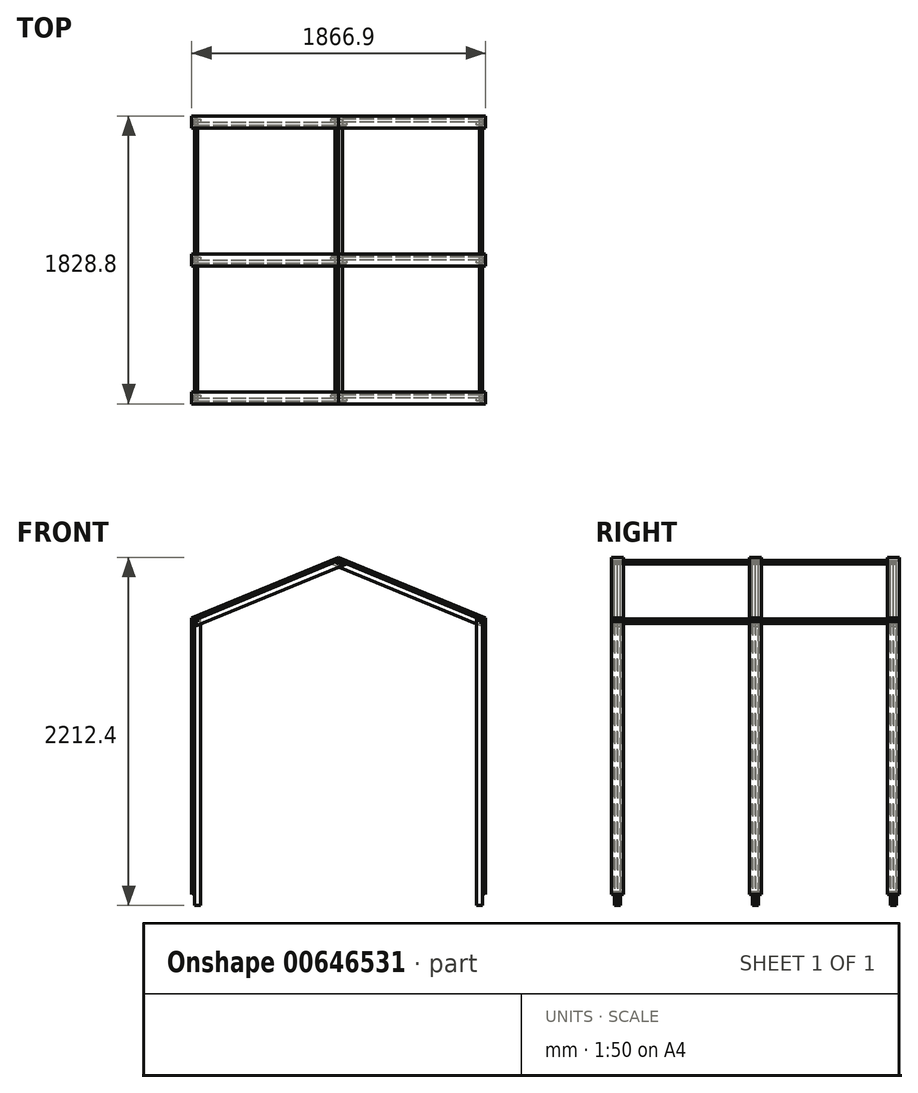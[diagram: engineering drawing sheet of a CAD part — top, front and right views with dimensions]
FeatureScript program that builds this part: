
annotation { "Feature Type Name" : "Feature", "Feature Type Description" : "" }
export const myFeature = defineFeature(function(context is Context, id is Id, definition is map)
    precondition{}
    {
        {
            var Q0;
            Q0=qCreatedBy(makeId("Front.planeOp"),FACE);
            var sketch = newSketch(context, id + "F0", { "sketchPlane" : qUnion([Q0])});
            skLineSegment(sketch, "E0", {"start": v(-914.4, 0) * mm, "end": v(914.4, 0) * mm, "construction": true});
            skLineSegment(sketch, "E1", {"start": v(914.4, 0) * mm, "end": v(914.4, -378.76) * mm, "construction": true});
            skLineSegment(sketch, "E2", {"start": v(914.4, -378.76) * mm, "end": v(-914.4, -378.76) * mm, "construction": true});
            skLineSegment(sketch, "E3", {"start": v(-914.4, -378.76) * mm, "end": v(-914.4, 0) * mm, "construction": true});
            skLineSegment(sketch, "E4", {"start": v(914.4, -378.76) * mm, "end": v(0, 0) * mm});
            skLineSegment(sketch, "E5", {"start": v(0, 0) * mm, "end": v(-914.4, -378.76) * mm, "construction": true});
            skLineSegment(sketch, "E6", {"start": v(914.4, -378.76) * mm, "end": v(914.4, -420) * mm});
            skLineSegment(sketch, "E7", {"start": v(914.4, -420) * mm, "end": v(-49.78, -20.62) * mm});
            skLineSegment(sketch, "E8", {"start": v(-49.78, -20.62) * mm, "end": v(0, 0) * mm});
            skSolve(sketch);
        }
        {
            var Q0;
            Q0=makeQuery(id+"F0.imprint","IMPRINT",FACE,{"disambiguationData":[TD([[makeQuery(id+"F0.imprint","IMPRINT",EDGE,{"derivedFrom":sQuery(id+"F0.wireOp",EDGE,"E4")}),1.0]])]});
            extrude(context, id + "F1", {"entities" : qUnion([Q0]), "depth" : 19.05 * mm, "offsetDistance" : 25.4 * mm});
        }
        {
            var Q0;
            Q0=makeQuery(id+"F1.opExtrude","SWEPT_BODY",BODY,{"disambiguationData":[OSD([sQuery(id+"F0.wireOp",EDGE,"E4"),sQuery(id+"F0.wireOp",EDGE,"E6"),sQuery(id+"F0.wireOp",EDGE,"E7"),sQuery(id+"F0.wireOp",EDGE,"E8")])]});
            var Q1;
            Q1=makeQuery(id+"F1.opExtrude","CAP_VERTEX",VERTEX,{"disambiguationData":[OSD([sQuery(id+"F0.wireOp",EDGE,"E4"),sQuery(id+"F0.wireOp",EDGE,"E6")])],"isStart":true});
            var Q2;
            Q2=makeQuery(id+"F1.opExtrude","CAP_VERTEX",VERTEX,{"disambiguationData":[OSD([sQuery(id+"F0.wireOp",EDGE,"E4"),sQuery(id+"F0.wireOp",EDGE,"E6")])],"isStart":false});
            var Q3;
            Q3=makeQuery(id+"F1.opExtrude","CAP_EDGE",EDGE,{"disambiguationData":[OSD([sQuery(id+"F0.wireOp",EDGE,"E6")])],"isStart":false});
            transform(context, id + "F2", {"entities" : qUnion([Q0]), "transformType" : TransformType.ROTATION, "transformAxis" : qUnion([Q3]), "angle" : 180 * degree, "makeCopy" : true});
        }
        {
            var Q0;
            Q0=makeQuery(id+"F2.opPattern","COPY",BODY,{"derivedFrom":makeQuery(id+"F1.opExtrude","SWEPT_BODY",BODY,{"disambiguationData":[OSD([sQuery(id+"F0.wireOp",EDGE,"E4"),sQuery(id+"F0.wireOp",EDGE,"E6"),sQuery(id+"F0.wireOp",EDGE,"E7"),sQuery(id+"F0.wireOp",EDGE,"E8")])]}),"instanceName":"1"});
            var Q1;
            Q1=makeQuery(id+"F2.opPattern","COPY",VERTEX,{"derivedFrom":makeQuery(id+"F1.opExtrude","CAP_VERTEX",VERTEX,{"disambiguationData":[OSD([sQuery(id+"F0.wireOp",EDGE,"E4"),sQuery(id+"F0.wireOp",EDGE,"E8")])],"isStart":false}),"instanceName":"1"});
            var Q2;
            Q2=makeQuery(id+"F1.opExtrude","CAP_VERTEX",VERTEX,{"disambiguationData":[OSD([sQuery(id+"F0.wireOp",EDGE,"E4"),sQuery(id+"F0.wireOp",EDGE,"E8")])],"isStart":false});
            transform(context, id + "F3", {"entities" : qUnion([Q0]), "transformType" : TransformType.TRANSLATION_ENTITY, "oppositeDirectionEntity" : false, "transformLine" : qUnion([Q1, Q2]), "makeCopy" : false});
        }
        {
            var Q0;
            Q0=makeQuery(id+"F1.opExtrude","CAP_FACE",FACE,{"disambiguationData":[OSD([sQuery(id+"F0.wireOp",EDGE,"E4"),sQuery(id+"F0.wireOp",EDGE,"E6"),sQuery(id+"F0.wireOp",EDGE,"E7"),sQuery(id+"F0.wireOp",EDGE,"E8")])],"isStart":false});
            var sketch = newSketch(context, id + "F4", { "sketchPlane" : qUnion([Q0])});
            skLineSegment(sketch, "E9", {"start": v(914.4, -378.76) * mm, "end": v(914.4, -2191.78) * mm});
            skLineSegment(sketch, "E10", {"start": v(914.4, -2191.78) * mm, "end": v(876.3, -2191.78) * mm});
            skLineSegment(sketch, "E11", {"start": v(876.3, -2191.78) * mm, "end": v(876.3, -362.98) * mm});
            skLineSegment(sketch, "E12", {"start": v(876.3, -362.98) * mm, "end": v(914.4, -378.76) * mm});
            skSolve(sketch);
        }
        {
            var Q0;
            {var subQ3=sQuery(id+"F4.wireOp",EDGE,"E10");Q0=makeQuery(id+"F4.imprint","IMPRINT",FACE,{"disambiguationData":[TD([[makeQuery(id+"F4.imprint","IMPRINT",EDGE,{"derivedFrom":subQ3}),-1.0]])]});}
            var Q1;
            {var subQ0=sQuery(id+"F4.wireOp",EDGE,"E12");Q1=makeQuery(id+"F4.imprint","IMPRINT",FACE,{"disambiguationData":[TD([[makeQuery(id+"F4.imprint","IMPRINT",EDGE,{"derivedFrom":subQ0}),1.0]])]});}
            extrude(context, id + "F5", {"entities" : qUnion([Q0, Q1]), "depth" : 19.05 * mm, "offsetDistance" : 25.4 * mm});
        }
        {
            var Q0;
            Q0=makeQuery(id+"F5.opExtrude","SWEPT_BODY",BODY,{"disambiguationData":[OSD([sQuery(id+"F4.wireOp",EDGE,"E9"),sQuery(id+"F4.wireOp",EDGE,"E10"),sQuery(id+"F4.wireOp",EDGE,"E11"),sQuery(id+"F4.wireOp",EDGE,"E12")])]});
            var Q1;
            Q1=makeQuery(id+"F5.opExtrude","CAP_EDGE",EDGE,{"disambiguationData":[OSD([sQuery(id+"F4.wireOp",EDGE,"E9")])],"isStart":true});
            transform(context, id + "F6", {"entities" : qUnion([Q0]), "transformType" : TransformType.ROTATION, "transformAxis" : qUnion([Q1]), "angle" : 180 * degree, "makeCopy" : true});
        }
        {
            var Q0;
            Q0=makeQuery(id+"F6.opPattern","COPY",BODY,{"derivedFrom":makeQuery(id+"F5.opExtrude","SWEPT_BODY",BODY,{"disambiguationData":[OSD([sQuery(id+"F4.wireOp",EDGE,"E9"),sQuery(id+"F4.wireOp",EDGE,"E10"),sQuery(id+"F4.wireOp",EDGE,"E11"),sQuery(id+"F4.wireOp",EDGE,"E12")])]}),"instanceName":"1"});
            var Q1;
            Q1=makeQuery(id+"F5.opExtrude","CAP_VERTEX",VERTEX,{"disambiguationData":[OSD([sQuery(id+"F4.wireOp",EDGE,"E9"),sQuery(id+"F4.wireOp",EDGE,"E12")])],"isStart":true});
            var Q2;
            Q2=makeQuery(id+"F2.opPattern","COPY",VERTEX,{"derivedFrom":makeQuery(id+"F1.opExtrude","CAP_VERTEX",VERTEX,{"disambiguationData":[OSD([sQuery(id+"F0.wireOp",EDGE,"E4"),sQuery(id+"F0.wireOp",EDGE,"E6")])],"isStart":false}),"instanceName":"1"});
            transform(context, id + "F7", {"entities" : qUnion([Q0]), "transformType" : TransformType.TRANSLATION_ENTITY, "oppositeDirectionEntity" : false, "transformLine" : qUnion([Q1, Q2]), "makeCopy" : false});
        }
        {
            var Q0;
            Q0=qCreatedBy(makeId("Front.planeOp"),FACE);
            var sketch = newSketch(context, id + "F8", { "sketchPlane" : qUnion([Q0])});
            skLineSegment(sketch, "E13.0", {"start": v(914.4, -378.76) * mm, "end": v(914.4, -2191.78) * mm});
            skLineSegment(sketch, "E14.0", {"start": v(914.4, -378.76) * mm, "end": v(0, 0) * mm});
            skLineSegment(sketch, "E15.0", {"start": v(-914.4, -378.76) * mm, "end": v(0, 0) * mm});
            skLineSegment(sketch, "E16.0", {"start": v(-914.4, -378.76) * mm, "end": v(-914.4, -2191.78) * mm});
            skLineSegment(sketch, "E17", {"start": v(914.4, -2191.78) * mm, "end": v(933.45, -2191.78) * mm});
            skLineSegment(sketch, "E18", {"start": v(933.45, -2191.78) * mm, "end": v(933.45, -2121.93) * mm});
            skLineSegment(sketch, "E19", {"start": v(933.45, -2121.93) * mm, "end": v(914.4, -2102.88) * mm});
            skLineSegment(sketch, "E20", {"start": v(933.45, -2121.93) * mm, "end": v(933.45, -386.65) * mm});
            skLineSegment(sketch, "E21", {"start": v(933.45, -386.65) * mm, "end": v(914.4, -378.76) * mm});
            skLineSegment(sketch, "E22", {"start": v(933.45, -386.65) * mm, "end": v(933.45, -366.03) * mm});
            skLineSegment(sketch, "E23", {"start": v(933.45, -366.03) * mm, "end": v(0, 20.62) * mm});
            skLineSegment(sketch, "E24", {"start": v(0, 20.62) * mm, "end": v(0, 0) * mm});
            skSolve(sketch);
        }
        {
            var Q0;
            Q0=makeQuery(id+"F8.imprint","IMPRINT",FACE,{"disambiguationData":[TD([[makeQuery(id+"F8.imprint","IMPRINT",EDGE,{"derivedFrom":sQuery(id+"F8.wireOp",EDGE,"E14.0")}),-1.0]])]});
            extrude(context, id + "F9", {"entities" : qUnion([Q0]), "depth" : 76.2 * mm, "offsetDistance" : 25.4 * mm});
        }
        {
            var Q0;
            {var subQ2=sQuery(id+"F8.wireOp",EDGE,"E19");Q0=makeQuery(id+"F8.imprint","IMPRINT",FACE,{"disambiguationData":[TD([[makeQuery(id+"F8.imprint","IMPRINT",EDGE,{"derivedFrom":subQ2}),-1.0]])]});}
            extrude(context, id + "F10", {"entities" : qUnion([Q0]), "depth" : 76.2 * mm, "offsetDistance" : 25.4 * mm});
        }
        {
            var Q0;
            Q0=makeQuery(id+"F9.opExtrude","SWEPT_BODY",BODY,{"disambiguationData":[OSD([sQuery(id+"F8.wireOp",EDGE,"E14.0"),sQuery(id+"F8.wireOp",EDGE,"E21"),sQuery(id+"F8.wireOp",EDGE,"E22"),sQuery(id+"F8.wireOp",EDGE,"E23"),sQuery(id+"F8.wireOp",EDGE,"E24")])]});
            var Q1;
            Q1=makeQuery(id+"F10.opExtrude","SWEPT_BODY",BODY,{"disambiguationData":[OSD([sQuery(id+"F8.wireOp",EDGE,"E13.0"),sQuery(id+"F8.wireOp",EDGE,"E19"),sQuery(id+"F8.wireOp",EDGE,"E20"),sQuery(id+"F8.wireOp",EDGE,"E21")])]});
            var Q2;
            Q2=sQuery(id+"F8.wireOp",EDGE,"E24");
            transform(context, id + "F11", {"entities" : qUnion([Q0, Q1]), "transformType" : TransformType.ROTATION, "transformAxis" : qUnion([Q2]), "angle" : 180 * degree, "makeCopy" : true});
        }
        {
            var Q0;
            Q0=makeQuery(id+"F11.opPattern","COPY",BODY,{"derivedFrom":makeQuery(id+"F10.opExtrude","SWEPT_BODY",BODY,{"disambiguationData":[OSD([sQuery(id+"F8.wireOp",EDGE,"E13.0"),sQuery(id+"F8.wireOp",EDGE,"E19"),sQuery(id+"F8.wireOp",EDGE,"E20"),sQuery(id+"F8.wireOp",EDGE,"E21")])]}),"instanceName":"1"});
            var Q1;
            Q1=makeQuery(id+"F11.opPattern","COPY",BODY,{"derivedFrom":makeQuery(id+"F9.opExtrude","SWEPT_BODY",BODY,{"disambiguationData":[OSD([sQuery(id+"F8.wireOp",EDGE,"E14.0"),sQuery(id+"F8.wireOp",EDGE,"E21"),sQuery(id+"F8.wireOp",EDGE,"E22"),sQuery(id+"F8.wireOp",EDGE,"E23"),sQuery(id+"F8.wireOp",EDGE,"E24")])]}),"instanceName":"1"});
            var Q2;
            Q2=sQuery(id+"F8.wireOp",VERTEX,"E24.start");
            var Q3;
            Q3=makeQuery(id+"F9.opExtrude","CAP_VERTEX",VERTEX,{"disambiguationData":[OSD([sQuery(id+"F8.wireOp",EDGE,"E23"),sQuery(id+"F8.wireOp",EDGE,"E24")])],"isStart":false});
            transform(context, id + "F12", {"entities" : qUnion([Q0, Q1]), "transformType" : TransformType.TRANSLATION_ENTITY, "oppositeDirectionEntity" : false, "transformLine" : qUnion([Q2, Q3]), "makeCopy" : false});
        }
        {
            var Q0;
            Q0=makeQuery(id+"F11.opPattern","COPY",BODY,{"derivedFrom":makeQuery(id+"F10.opExtrude","SWEPT_BODY",BODY,{"disambiguationData":[OSD([sQuery(id+"F8.wireOp",EDGE,"E13.0"),sQuery(id+"F8.wireOp",EDGE,"E19"),sQuery(id+"F8.wireOp",EDGE,"E20"),sQuery(id+"F8.wireOp",EDGE,"E21")])]}),"instanceName":"1"});
            var Q1;
            Q1=makeQuery(id+"F11.opPattern","COPY",BODY,{"derivedFrom":makeQuery(id+"F9.opExtrude","SWEPT_BODY",BODY,{"disambiguationData":[OSD([sQuery(id+"F8.wireOp",EDGE,"E14.0"),sQuery(id+"F8.wireOp",EDGE,"E21"),sQuery(id+"F8.wireOp",EDGE,"E22"),sQuery(id+"F8.wireOp",EDGE,"E23"),sQuery(id+"F8.wireOp",EDGE,"E24")])]}),"instanceName":"1"});
            var Q2;
            Q2=makeQuery(id+"F10.opExtrude","SWEPT_BODY",BODY,{"disambiguationData":[OSD([sQuery(id+"F8.wireOp",EDGE,"E13.0"),sQuery(id+"F8.wireOp",EDGE,"E19"),sQuery(id+"F8.wireOp",EDGE,"E20"),sQuery(id+"F8.wireOp",EDGE,"E21")])]});
            var Q3;
            Q3=makeQuery(id+"F9.opExtrude","SWEPT_BODY",BODY,{"disambiguationData":[OSD([sQuery(id+"F8.wireOp",EDGE,"E14.0"),sQuery(id+"F8.wireOp",EDGE,"E21"),sQuery(id+"F8.wireOp",EDGE,"E22"),sQuery(id+"F8.wireOp",EDGE,"E23"),sQuery(id+"F8.wireOp",EDGE,"E24")])]});
            transform(context, id + "F13", {"entities" : qUnion([Q0, Q1, Q2, Q3]), "transformType" : TransformType.TRANSLATION_3D, "dx" : 0 * mm, "dy" : 19.05 * mm, "dz" : 0 * mm, "makeCopy" : false});
        }
        {
            var Q0;
            Q0=makeQuery(id+"F2.opPattern","COPY",FACE,{"derivedFrom":makeQuery(id+"F1.opExtrude","CAP_FACE",FACE,{"disambiguationData":[OSD([sQuery(id+"F0.wireOp",EDGE,"E4"),sQuery(id+"F0.wireOp",EDGE,"E6"),sQuery(id+"F0.wireOp",EDGE,"E7"),sQuery(id+"F0.wireOp",EDGE,"E8")])],"isStart":true}),"instanceName":"1"});
            var sketch = newSketch(context, id + "F14", { "sketchPlane" : qUnion([Q0])});
            skLineSegment(sketch, "E25", {"start": v(0, 0) * mm, "end": v(-24.9, -10.3) * mm});
            skLineSegment(sketch, "E26", {"start": v(-24.9, -10.3) * mm, "end": v(0, -20.62) * mm});
            skLineSegment(sketch, "E27", {"start": v(0, -20.62) * mm, "end": v(24.9, -10.3) * mm});
            skPoint(sketch, "E27.endSnap0", {"position": v(24.9, -10.3) * mm});
            skLineSegment(sketch, "E28", {"start": v(24.9, -10.3) * mm, "end": v(0, 0) * mm});
            skSolve(sketch);
        }
        {
            var Q0;
            Q0=makeQuery(id+"F14.imprint","IMPRINT",FACE,{"disambiguationData":[TD([[makeQuery(id+"F14.imprint","IMPRINT",EDGE,{"derivedFrom":sQuery(id+"F14.wireOp",EDGE,"E25")}),-1.0]])]});
            extrude(context, id + "F15", {"entities" : qUnion([Q0]), "operationType" : NewBodyOperationType.REMOVE, "endBound" : BoundingType.THROUGH_ALL, "oppositeDirection" : true, "depth" : 25.4 * mm, "offsetDistance" : 25.4 * mm});
        }
        {
            var Q0;
            Q0=makeQuery(id+"F5.opExtrude","CAP_FACE",FACE,{"disambiguationData":[OSD([sQuery(id+"F4.wireOp",EDGE,"E9"),sQuery(id+"F4.wireOp",EDGE,"E10"),sQuery(id+"F4.wireOp",EDGE,"E11"),sQuery(id+"F4.wireOp",EDGE,"E12")])],"isStart":false});
            var sketch = newSketch(context, id + "F16", { "sketchPlane" : qUnion([Q0])});
            skLineSegment(sketch, "E29", {"start": v(914.4, -378.76) * mm, "end": v(895.35, -370.87) * mm});
            skLineSegment(sketch, "E30", {"start": v(895.35, -370.87) * mm, "end": v(895.35, -391.49) * mm});
            skLineSegment(sketch, "E31", {"start": v(895.35, -391.49) * mm, "end": v(914.4, -399.38) * mm});
            skLineSegment(sketch, "E32", {"start": v(914.4, -399.38) * mm, "end": v(914.4, -378.76) * mm});
            skSolve(sketch);
        }
        {
            var Q0;
            Q0=makeQuery(id+"F16.imprint","IMPRINT",FACE,{"disambiguationData":[TD([[makeQuery(id+"F16.imprint","IMPRINT",EDGE,{"derivedFrom":sQuery(id+"F16.wireOp",EDGE,"E29")}),1.0]])]});
            extrude(context, id + "F17", {"entities" : qUnion([Q0]), "operationType" : NewBodyOperationType.REMOVE, "endBound" : BoundingType.THROUGH_ALL, "oppositeDirection" : true, "depth" : 25.4 * mm, "offsetDistance" : 25.4 * mm});
        }
        {
            var Q0;
            Q0=makeQuery(id+"F6.opPattern","COPY",FACE,{"derivedFrom":makeQuery(id+"F5.opExtrude","CAP_FACE",FACE,{"disambiguationData":[OSD([sQuery(id+"F4.wireOp",EDGE,"E9"),sQuery(id+"F4.wireOp",EDGE,"E10"),sQuery(id+"F4.wireOp",EDGE,"E11"),sQuery(id+"F4.wireOp",EDGE,"E12")])],"isStart":false}),"instanceName":"1"});
            var sketch = newSketch(context, id + "F18", { "sketchPlane" : qUnion([Q0])});
            skLineSegment(sketch, "E33", {"start": v(914.4, -378.76) * mm, "end": v(895.35, -370.87) * mm});
            skLineSegment(sketch, "E34", {"start": v(895.35, -370.87) * mm, "end": v(895.35, -391.49) * mm});
            skLineSegment(sketch, "E35", {"start": v(895.35, -391.49) * mm, "end": v(914.4, -399.38) * mm});
            skLineSegment(sketch, "E36", {"start": v(914.4, -399.38) * mm, "end": v(914.4, -378.76) * mm});
            skSolve(sketch);
        }
        {
            var Q0;
            Q0=makeQuery(id+"F18.imprint","IMPRINT",FACE,{"disambiguationData":[TD([[makeQuery(id+"F18.imprint","IMPRINT",EDGE,{"derivedFrom":sQuery(id+"F18.wireOp",EDGE,"E33")}),1.0]])]});
            extrude(context, id + "F19", {"entities" : qUnion([Q0]), "operationType" : NewBodyOperationType.REMOVE, "endBound" : BoundingType.THROUGH_ALL, "oppositeDirection" : true, "depth" : 25.4 * mm, "offsetDistance" : 25.4 * mm});
        }
        {
            var Q0;
            Q0=makeQuery(id+"F1.opExtrude","CAP_FACE",FACE,{"disambiguationData":[OSD([sQuery(id+"F0.wireOp",EDGE,"E4"),sQuery(id+"F0.wireOp",EDGE,"E6"),sQuery(id+"F0.wireOp",EDGE,"E7"),sQuery(id+"F0.wireOp",EDGE,"E8")])],"isStart":false});
            var sketch = newSketch(context, id + "F20", { "sketchPlane" : qUnion([Q0])});
            skLineSegment(sketch, "E37", {"start": v(895.35, -391.49) * mm, "end": v(895.35, -370.87) * mm});
            skLineSegment(sketch, "E38", {"start": v(895.35, -370.87) * mm, "end": v(914.4, -378.76) * mm});
            skLineSegment(sketch, "E39", {"start": v(914.4, -378.76) * mm, "end": v(914.4, -399.38) * mm});
            skLineSegment(sketch, "E40", {"start": v(914.4, -399.38) * mm, "end": v(895.35, -391.49) * mm});
            skSolve(sketch);
        }
        {
            var Q0;
            Q0=makeQuery(id+"F20.imprint","IMPRINT",FACE,{"disambiguationData":[TD([[makeQuery(id+"F20.imprint","IMPRINT",EDGE,{"derivedFrom":sQuery(id+"F20.wireOp",EDGE,"E37")}),1.0]])]});
            extrude(context, id + "F21", {"entities" : qUnion([Q0]), "depth" : 895.35 * mm, "offsetDistance" : 25.4 * mm, "hasSecondDirection" : true, "secondDirectionOppositeDirection" : true, "secondDirectionDepth" : 895.35 * mm});
        }
        {
            var Q0;
            Q0=makeQuery(id+"F2.opPattern","COPY",FACE,{"derivedFrom":makeQuery(id+"F1.opExtrude","CAP_FACE",FACE,{"disambiguationData":[OSD([sQuery(id+"F0.wireOp",EDGE,"E4"),sQuery(id+"F0.wireOp",EDGE,"E6"),sQuery(id+"F0.wireOp",EDGE,"E7"),sQuery(id+"F0.wireOp",EDGE,"E8")])],"isStart":false}),"instanceName":"1"});
            var sketch = newSketch(context, id + "F22", { "sketchPlane" : qUnion([Q0])});
            skLineSegment(sketch, "E41", {"start": v(895.35, -391.49) * mm, "end": v(895.35, -370.87) * mm});
            skLineSegment(sketch, "E42", {"start": v(895.35, -370.87) * mm, "end": v(914.4, -378.76) * mm});
            skLineSegment(sketch, "E43", {"start": v(914.4, -378.76) * mm, "end": v(914.4, -399.38) * mm});
            skLineSegment(sketch, "E44", {"start": v(914.4, -399.38) * mm, "end": v(895.35, -391.49) * mm});
            skSolve(sketch);
        }
        {
            var Q0;
            Q0=makeQuery(id+"F22.imprint","IMPRINT",FACE,{"disambiguationData":[TD([[makeQuery(id+"F22.imprint","IMPRINT",EDGE,{"derivedFrom":sQuery(id+"F22.wireOp",EDGE,"E41")}),1.0]])]});
            extrude(context, id + "F23", {"entities" : qUnion([Q0]), "depth" : 895.35 * mm, "offsetDistance" : 25.4 * mm, "hasSecondDirection" : true, "secondDirectionOppositeDirection" : true, "secondDirectionDepth" : 895.35 * mm});
        }
        {
            var Q0;
            Q0=makeQuery(id+"F1.opExtrude","CAP_FACE",FACE,{"disambiguationData":[OSD([sQuery(id+"F0.wireOp",EDGE,"E4"),sQuery(id+"F0.wireOp",EDGE,"E6"),sQuery(id+"F0.wireOp",EDGE,"E7"),sQuery(id+"F0.wireOp",EDGE,"E8")])],"isStart":false});
            var sketch = newSketch(context, id + "F24", { "sketchPlane" : qUnion([Q0])});
            skLineSegment(sketch, "E45", {"start": v(-24.9, -10.3) * mm, "end": v(0, -20.62) * mm});
            skLineSegment(sketch, "E46", {"start": v(0, -20.62) * mm, "end": v(24.9, -10.3) * mm});
            skLineSegment(sketch, "E47", {"start": v(24.9, -10.3) * mm, "end": v(0, 0) * mm});
            skLineSegment(sketch, "E48", {"start": v(0, 0) * mm, "end": v(-24.9, -10.3) * mm});
            skSolve(sketch);
        }
        {
            var Q0;
            Q0=makeQuery(id+"F24.imprint","IMPRINT",FACE,{"disambiguationData":[TD([[makeQuery(id+"F24.imprint","IMPRINT",EDGE,{"derivedFrom":sQuery(id+"F24.wireOp",EDGE,"E45")}),1.0]])]});
            extrude(context, id + "F25", {"entities" : qUnion([Q0]), "depth" : 895.35 * mm, "offsetDistance" : 25.4 * mm, "hasSecondDirection" : true, "secondDirectionOppositeDirection" : true, "secondDirectionDepth" : 895.35 * mm});
        }
        {
            var Q0;
            Q0=makeQuery(id+"F2.opPattern","COPY",BODY,{"derivedFrom":makeQuery(id+"F1.opExtrude","SWEPT_BODY",BODY,{"disambiguationData":[OSD([sQuery(id+"F0.wireOp",EDGE,"E4"),sQuery(id+"F0.wireOp",EDGE,"E6"),sQuery(id+"F0.wireOp",EDGE,"E7"),sQuery(id+"F0.wireOp",EDGE,"E8")])]}),"instanceName":"1"});
            var Q1;
            Q1=makeQuery(id+"F11.opPattern","COPY",BODY,{"derivedFrom":makeQuery(id+"F9.opExtrude","SWEPT_BODY",BODY,{"disambiguationData":[OSD([sQuery(id+"F8.wireOp",EDGE,"E14.0"),sQuery(id+"F8.wireOp",EDGE,"E21"),sQuery(id+"F8.wireOp",EDGE,"E22"),sQuery(id+"F8.wireOp",EDGE,"E23"),sQuery(id+"F8.wireOp",EDGE,"E24")])]}),"instanceName":"1"});
            var Q2;
            Q2=makeQuery(id+"F6.opPattern","COPY",BODY,{"derivedFrom":makeQuery(id+"F5.opExtrude","SWEPT_BODY",BODY,{"disambiguationData":[OSD([sQuery(id+"F4.wireOp",EDGE,"E9"),sQuery(id+"F4.wireOp",EDGE,"E10"),sQuery(id+"F4.wireOp",EDGE,"E11"),sQuery(id+"F4.wireOp",EDGE,"E12")])]}),"instanceName":"1"});
            var Q3;
            Q3=makeQuery(id+"F1.opExtrude","SWEPT_BODY",BODY,{"disambiguationData":[OSD([sQuery(id+"F0.wireOp",EDGE,"E4"),sQuery(id+"F0.wireOp",EDGE,"E6"),sQuery(id+"F0.wireOp",EDGE,"E7"),sQuery(id+"F0.wireOp",EDGE,"E8")])]});
            var Q4;
            Q4=makeQuery(id+"F9.opExtrude","SWEPT_BODY",BODY,{"disambiguationData":[OSD([sQuery(id+"F8.wireOp",EDGE,"E14.0"),sQuery(id+"F8.wireOp",EDGE,"E21"),sQuery(id+"F8.wireOp",EDGE,"E22"),sQuery(id+"F8.wireOp",EDGE,"E23"),sQuery(id+"F8.wireOp",EDGE,"E24")])]});
            var Q5;
            Q5=makeQuery(id+"F10.opExtrude","SWEPT_BODY",BODY,{"disambiguationData":[OSD([sQuery(id+"F8.wireOp",EDGE,"E13.0"),sQuery(id+"F8.wireOp",EDGE,"E19"),sQuery(id+"F8.wireOp",EDGE,"E20"),sQuery(id+"F8.wireOp",EDGE,"E21")])]});
            var Q6;
            Q6=makeQuery(id+"F5.opExtrude","SWEPT_BODY",BODY,{"disambiguationData":[OSD([sQuery(id+"F4.wireOp",EDGE,"E9"),sQuery(id+"F4.wireOp",EDGE,"E10"),sQuery(id+"F4.wireOp",EDGE,"E11"),sQuery(id+"F4.wireOp",EDGE,"E12")])]});
            var Q7;
            Q7=makeQuery(id+"F11.opPattern","COPY",BODY,{"derivedFrom":makeQuery(id+"F10.opExtrude","SWEPT_BODY",BODY,{"disambiguationData":[OSD([sQuery(id+"F8.wireOp",EDGE,"E13.0"),sQuery(id+"F8.wireOp",EDGE,"E19"),sQuery(id+"F8.wireOp",EDGE,"E20"),sQuery(id+"F8.wireOp",EDGE,"E21")])]}),"instanceName":"1"});
            var Q8;
            Q8=makeQuery(id+"F17.boolean.opBoolean","COPY",VERTEX,{"derivedFrom":makeQuery(id+"F17.opExtrude","CAP_VERTEX",VERTEX,{"disambiguationData":[OSD([sQuery(id+"F16.wireOp",EDGE,"E30"),sQuery(id+"F16.wireOp",EDGE,"E31")])],"isStart":true})});
            var Q9;
            Q9=makeQuery(id+"F21.opExtrude","CAP_VERTEX",VERTEX,{"disambiguationData":[OSD([sQuery(id+"F20.wireOp",EDGE,"E37"),sQuery(id+"F20.wireOp",EDGE,"E40")])],"isStart":false});
            transform(context, id + "F26", {"entities" : qUnion([Q0, Q1, Q2, Q3, Q4, Q5, Q6, Q7]), "transformType" : TransformType.TRANSLATION_ENTITY, "oppositeDirectionEntity" : false, "transformLine" : qUnion([Q8, Q9]), "makeCopy" : true});
        }
        {
            var Q0;
            Q0=makeQuery(id+"F1.opExtrude","SWEPT_BODY",BODY,{"disambiguationData":[OSD([sQuery(id+"F0.wireOp",EDGE,"E4"),sQuery(id+"F0.wireOp",EDGE,"E6"),sQuery(id+"F0.wireOp",EDGE,"E7"),sQuery(id+"F0.wireOp",EDGE,"E8")])]});
            var Q1;
            Q1=makeQuery(id+"F9.opExtrude","SWEPT_BODY",BODY,{"disambiguationData":[OSD([sQuery(id+"F8.wireOp",EDGE,"E14.0"),sQuery(id+"F8.wireOp",EDGE,"E21"),sQuery(id+"F8.wireOp",EDGE,"E22"),sQuery(id+"F8.wireOp",EDGE,"E23"),sQuery(id+"F8.wireOp",EDGE,"E24")])]});
            var Q2;
            Q2=makeQuery(id+"F6.opPattern","COPY",BODY,{"derivedFrom":makeQuery(id+"F5.opExtrude","SWEPT_BODY",BODY,{"disambiguationData":[OSD([sQuery(id+"F4.wireOp",EDGE,"E9"),sQuery(id+"F4.wireOp",EDGE,"E10"),sQuery(id+"F4.wireOp",EDGE,"E11"),sQuery(id+"F4.wireOp",EDGE,"E12")])]}),"instanceName":"1"});
            var Q3;
            Q3=makeQuery(id+"F2.opPattern","COPY",BODY,{"derivedFrom":makeQuery(id+"F1.opExtrude","SWEPT_BODY",BODY,{"disambiguationData":[OSD([sQuery(id+"F0.wireOp",EDGE,"E4"),sQuery(id+"F0.wireOp",EDGE,"E6"),sQuery(id+"F0.wireOp",EDGE,"E7"),sQuery(id+"F0.wireOp",EDGE,"E8")])]}),"instanceName":"1"});
            var Q4;
            Q4=makeQuery(id+"F10.opExtrude","SWEPT_BODY",BODY,{"disambiguationData":[OSD([sQuery(id+"F8.wireOp",EDGE,"E13.0"),sQuery(id+"F8.wireOp",EDGE,"E19"),sQuery(id+"F8.wireOp",EDGE,"E20"),sQuery(id+"F8.wireOp",EDGE,"E21")])]});
            var Q5;
            Q5=makeQuery(id+"F5.opExtrude","SWEPT_BODY",BODY,{"disambiguationData":[OSD([sQuery(id+"F4.wireOp",EDGE,"E9"),sQuery(id+"F4.wireOp",EDGE,"E10"),sQuery(id+"F4.wireOp",EDGE,"E11"),sQuery(id+"F4.wireOp",EDGE,"E12")])]});
            var Q6;
            Q6=makeQuery(id+"F11.opPattern","COPY",BODY,{"derivedFrom":makeQuery(id+"F10.opExtrude","SWEPT_BODY",BODY,{"disambiguationData":[OSD([sQuery(id+"F8.wireOp",EDGE,"E13.0"),sQuery(id+"F8.wireOp",EDGE,"E19"),sQuery(id+"F8.wireOp",EDGE,"E20"),sQuery(id+"F8.wireOp",EDGE,"E21")])]}),"instanceName":"1"});
            var Q7;
            Q7=makeQuery(id+"F11.opPattern","COPY",BODY,{"derivedFrom":makeQuery(id+"F9.opExtrude","SWEPT_BODY",BODY,{"disambiguationData":[OSD([sQuery(id+"F8.wireOp",EDGE,"E14.0"),sQuery(id+"F8.wireOp",EDGE,"E21"),sQuery(id+"F8.wireOp",EDGE,"E22"),sQuery(id+"F8.wireOp",EDGE,"E23"),sQuery(id+"F8.wireOp",EDGE,"E24")])]}),"instanceName":"1"});
            var Q8;
            Q8=makeQuery(id+"F17.boolean.opBoolean","INTERSECT",VERTEX,{"derivedFrom":[makeQuery(id+"F1.opExtrude","CAP_FACE",FACE,{"disambiguationData":[OSD([sQuery(id+"F0.wireOp",EDGE,"E4"),sQuery(id+"F0.wireOp",EDGE,"E6"),sQuery(id+"F0.wireOp",EDGE,"E7"),sQuery(id+"F0.wireOp",EDGE,"E8")])],"isStart":true}),makeQuery(id+"F17.opExtrude","SWEPT_FACE",FACE,{"disambiguationData":[OSD([sQuery(id+"F16.wireOp",EDGE,"E30")])]}),makeQuery(id+"F17.opExtrude","SWEPT_FACE",FACE,{"disambiguationData":[OSD([sQuery(id+"F16.wireOp",EDGE,"E31")])]})]});
            var Q9;
            Q9=makeQuery(id+"F21.opExtrude","CAP_VERTEX",VERTEX,{"disambiguationData":[OSD([sQuery(id+"F20.wireOp",EDGE,"E37"),sQuery(id+"F20.wireOp",EDGE,"E40")])],"isStart":true});
            transform(context, id + "F27", {"entities" : qUnion([Q0, Q1, Q2, Q3, Q4, Q5, Q6, Q7]), "transformType" : TransformType.TRANSLATION_ENTITY, "oppositeDirectionEntity" : false, "transformLine" : qUnion([Q8, Q9]), "makeCopy" : true});
        }
    });
